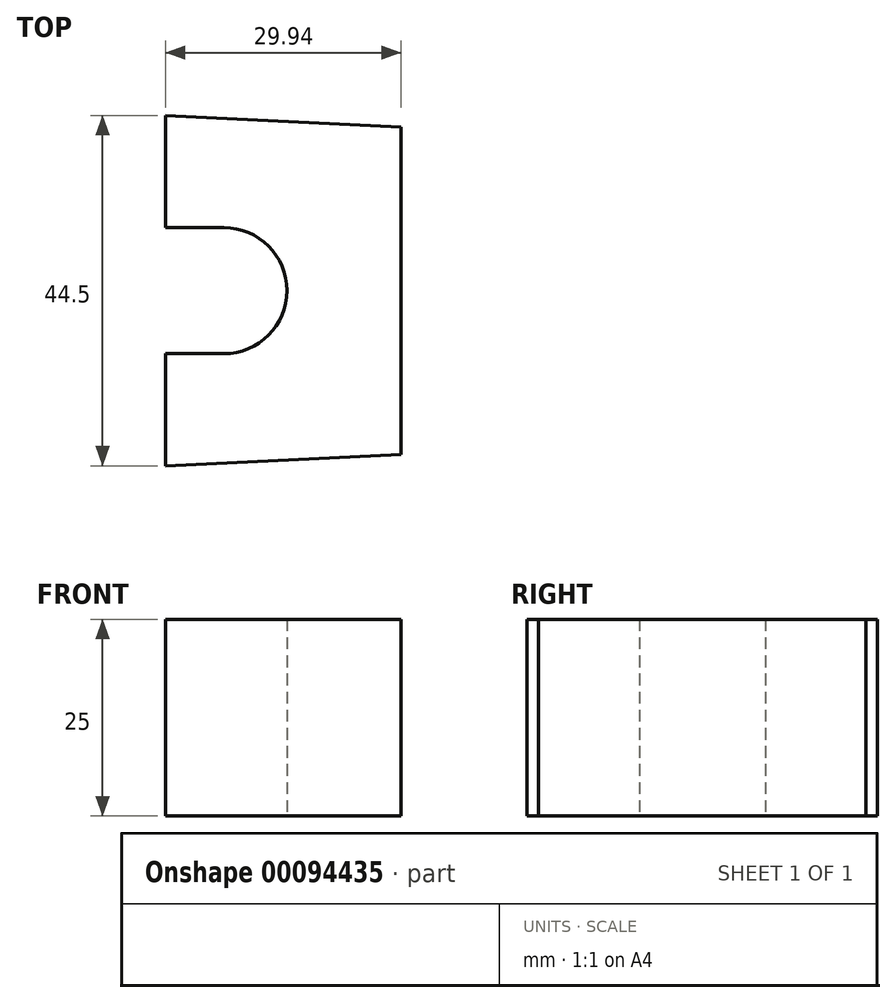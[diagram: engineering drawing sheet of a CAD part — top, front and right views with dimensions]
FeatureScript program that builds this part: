
annotation { "Feature Type Name" : "Feature", "Feature Type Description" : "" }
export const myFeature = defineFeature(function(context is Context, id is Id, definition is map)
    precondition{}
    {
        {
            var Q0;
            Q0=qCreatedBy(makeId("Top.planeOp"),FACE);
            var sketch = newSketch(context, id + "F0", { "sketchPlane" : qUnion([Q0])});
            skArc(sketch, "E0", {"start": v(1.86, -7.63) * mm, "mid": v(9.86, 0.37) * mm, "end": v(1.86, 8.37) * mm});
            skLineSegment(sketch, "E1", {"start": v(1.86, 8.37) * mm, "end": v(-5.57, 8.37) * mm});
            skLineSegment(sketch, "E2", {"start": v(1.86, -7.63) * mm, "end": v(-5.57, -7.63) * mm});
            skLineSegment(sketch, "E3", {"start": v(-5.57, 8.37) * mm, "end": v(-5.57, 22.62) * mm});
            skLineSegment(sketch, "E4", {"start": v(-5.57, -7.63) * mm, "end": v(-5.57, -21.88) * mm});
            skLineSegment(sketch, "E5.0", {"start": v(24.37, -20.43) * mm, "end": v(24.37, 21.16) * mm});
            skLineSegment(sketch, "E6", {"start": v(-5.57, 22.62) * mm, "end": v(24.37, 21.16) * mm});
            skLineSegment(sketch, "E7", {"start": v(-5.57, -21.88) * mm, "end": v(24.37, -20.43) * mm});
            skSolve(sketch);
        }
        {
            var Q0;
            Q0=makeQuery(id+"F0.imprint","IMPRINT",FACE,{"disambiguationData":[TD([[makeQuery(id+"F0.imprint","IMPRINT",EDGE,{"derivedFrom":sQuery(id+"F0.wireOp",EDGE,"E0")}),-1.0]])]});
            extrude(context, id + "F1", {"entities" : qUnion([Q0]), "depth" : 25 * mm});
        }
    });
